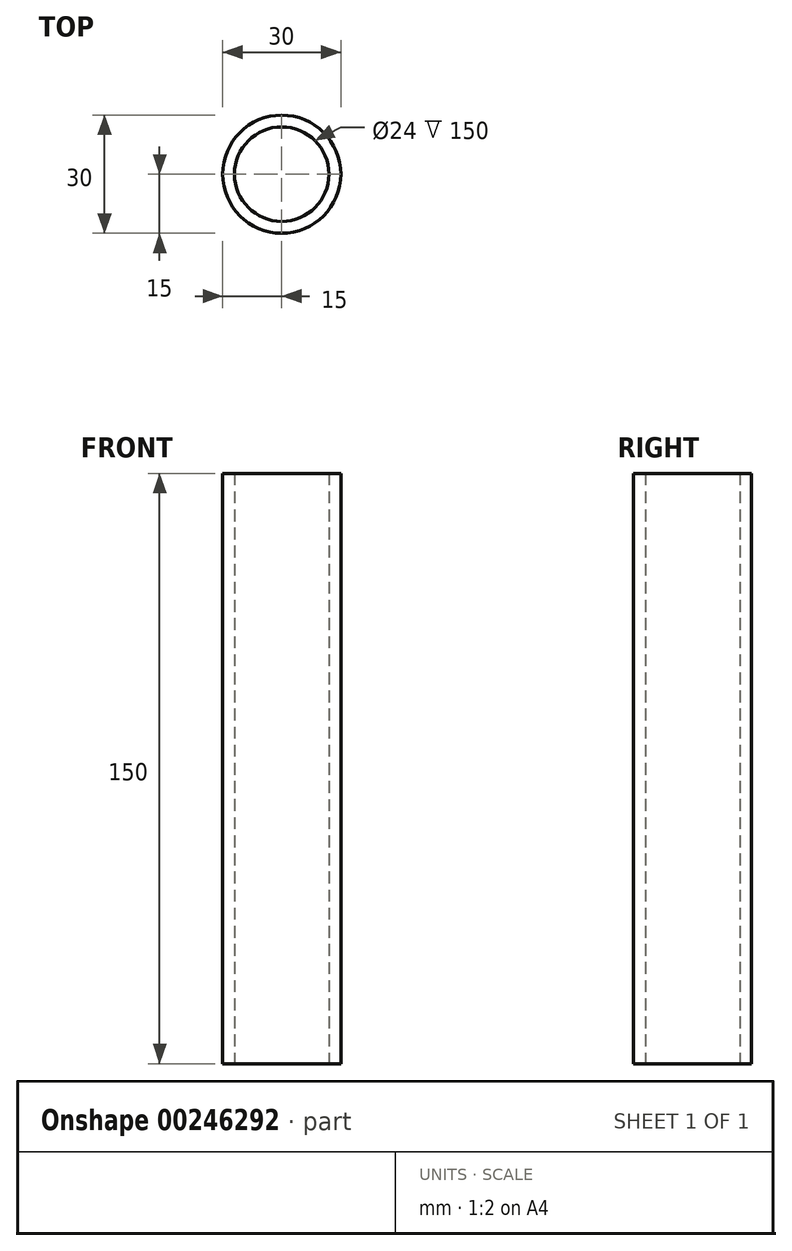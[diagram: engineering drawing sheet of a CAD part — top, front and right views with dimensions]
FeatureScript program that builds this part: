
annotation { "Feature Type Name" : "Feature", "Feature Type Description" : "" }
export const myFeature = defineFeature(function(context is Context, id is Id, definition is map)
    precondition{}
    {
        {
            var Q0;
            Q0=qCreatedBy(makeId("Top.planeOp"),FACE);
            var sketch = newSketch(context, id + "F0", { "sketchPlane" : qUnion([Q0])});
            skCircle(sketch, "E0", {"center": v(0, 0) * mm, "radius": 15 * mm});
            skCircle(sketch, "E1", {"center": v(0, 0) * mm, "radius": 12 * mm});
            skSolve(sketch);
        }
        {
            var Q0;
            Q0=makeQuery(id+"F0.imprint","IMPRINT",FACE,{"disambiguationData":[TD([[makeQuery(id+"F0.imprint","IMPRINT",EDGE,{"derivedFrom":sQuery(id+"F0.wireOp",EDGE,"E0")}),1.0]])]});
            extrude(context, id + "F1", {"entities" : qUnion([Q0]), "depth" : 150 * mm});
        }
    });
